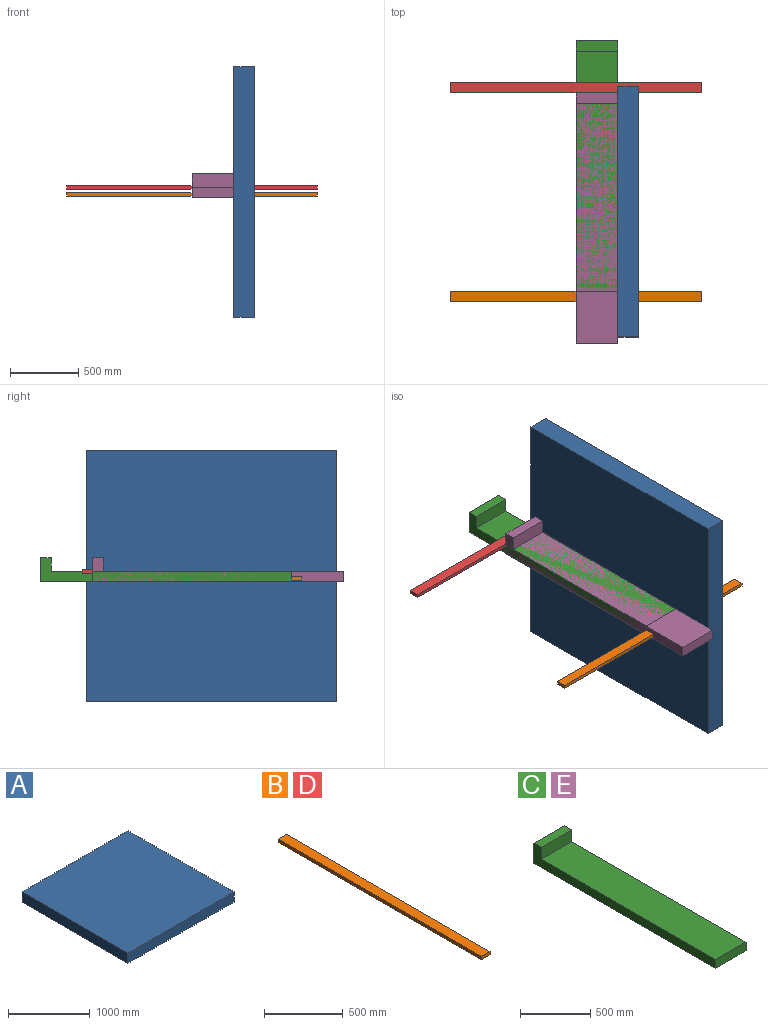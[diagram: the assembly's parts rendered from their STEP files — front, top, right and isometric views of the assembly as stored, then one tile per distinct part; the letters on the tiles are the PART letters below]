
ASSEMBLY  parts=5 mates=4
PART A: 6 faces, bbox 1828.8x1828.8x152.4 mm
  f0: plane 1828.8x152.4mm, normal (1,0,0), area 278709.1mm2, adj f1,f3,f4,f5
  f1: plane 1828.8x152.4mm, normal (0,1,0), area 278709.1mm2, adj f0,f2,f4,f5
  f2: plane 1828.8x152.4mm, normal (-1,0,0), area 278709.1mm2, adj f1,f3,f4,f5
  f3: plane 1828.8x152.4mm, normal (0,-1,0), area 278709.1mm2, adj f0,f2,f4,f5
  f4: plane 1828.8x1828.8mm, normal (0,0,1), area 3344509.4mm2, adj f0,f1,f2,f3
  f5: plane 1828.8x1828.8mm, normal (0,0,-1), area 3344509.4mm2, adj f0,f1,f2,f3
PART B: 6 faces, bbox 76.2x1828.8x25.4 mm
  f0: plane 76.2x25.4mm, normal (0,1,0), area 1935.5mm2, adj f1,f3,f4,f5
  f1: plane 1828.8x76.2mm, normal (0,0,1), area 139354.6mm2, adj f0,f2,f4,f5
  f2: plane 76.2x25.4mm, normal (0,-1,0), area 1935.5mm2, adj f1,f3,f4,f5
  f3: plane 1828.8x76.2mm, normal (0,0,-1), area 139354.6mm2, adj f0,f2,f4,f5
  f4: plane 1828.8x25.4mm, normal (1,0,0), area 46451.5mm2, adj f0,f1,f2,f3
  f5: plane 1828.8x25.4mm, normal (-1,0,0), area 46451.5mm2, adj f0,f1,f2,f3
PART C: 8 faces, bbox 304.8x1828.8x177.8 mm
  f0: plane 304.8x177.8mm, normal (0,1,0), area 54193.4mm2, adj f1,f5,f6,f7
  f1: plane 304.8x76.2mm, normal (0,0,1), area 23225.8mm2, adj f0,f2,f6,f7
  f2: plane 304.8x101.6mm, normal (0,-1,0), area 30967.7mm2, adj f1,f3,f6,f7
  f3: plane 1752.6x304.8mm, normal (0,0,1), area 534192.5mm2, adj f2,f4,f6,f7
  f4: plane 304.8x76.2mm, normal (0,-1,0), area 23225.8mm2, adj f3,f5,f6,f7
  f5: plane 1828.8x304.8mm, normal (0,0,-1), area 557418.2mm2, adj f0,f4,f6,f7
  f6: plane 1828.8x177.8mm, normal (1,0,0), area 147096.5mm2, adj f0,f1,f2,f3,f4,f5
  f7: plane 1828.8x177.8mm, normal (-1,0,0), area 147096.5mm2, adj f0,f1,f2,f3,f4,f5
PART D: same geometry as B
PART E: same geometry as C
PLACE A rot(axis=(-0.58,-0.58,0.58),120deg) t=(551.14,998.04,483.97)mm
PLACE B rot(axis=(0,0,-1),90deg) t=(93.94,418.52,466.59)mm
PLACE C t=(93.94,1332.92,479.29)mm
PLACE D rot(axis=(0.71,-0.71,0),180deg) t=(93.94,1942.52,517.39)mm
PLACE E t=(93.94,951.92,479.29)mm
MATE fastened A.f4 <-> E.f6  axis (-1,0,0) through (398.74,998.04,483.97)mm
MATE fastened B.f5 <-> C.f4  axis (0,1,0) through (93.94,418.52,466.59)mm
MATE fastened D.f4 <-> E.f0  axis (0,-1,0) through (93.94,1866.32,517.39)mm
MATE fastened C.f6 <-> A.f4  axis (1,0,0) through (398.74,1379.04,483.97)mm
